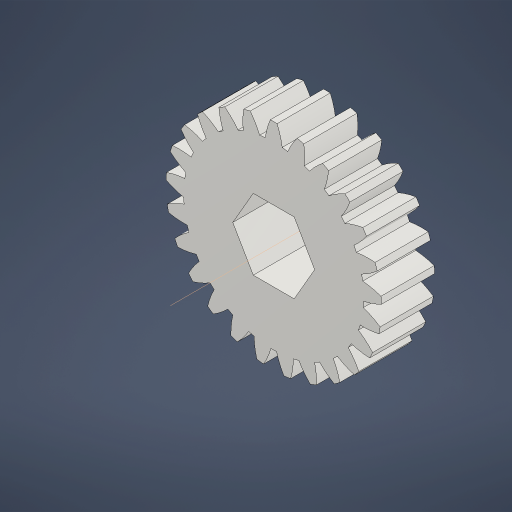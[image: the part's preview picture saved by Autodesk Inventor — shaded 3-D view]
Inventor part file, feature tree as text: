
AUTODESK INVENTOR PART (.ipt)
format: ipt  version: 2024.3 (Build 283343000, 343)  size: 343,552 bytes
history: native  units: mm (DEFAULTED — no unit token found)
features: plane x3, other x3, extrude x2, sketch x2
ambient origin geometry x8: Origin, YZ Plane, XZ Plane, XY Plane, X Axis, Y Axis, Z Axis, Center Point
bodies: Solid1 (feature_tree)
feature tree (10):
  extrude  "Extrusion1"  Depth=9.525mm TaperAngle=0.0deg
  plane  "Work Plane1"
  plane  "Work Plane2"
  plane  "Work Plane3"
  other  "Spur Gear"
  extrude  "Extrusion2"  Depth=12.7mm TaperAngle=0.0deg
  sketch  "Sketch1"  dims[d0=38.593216mm d1=9.525mm d2=0.0mm]
  other  "Srf1"
  sketch  "Sketch3"  dims[d3=35.277778mm d4=76.2mm d5=0.0mm d6=0.0mm d7=1.256637mm d9=0.0mm d14=0.0mm d15=88.441052mm d16=0.0mm d17=0.0mm d18=0.0mm d19=88.441052mm d20=12.7mm d21=0.0mm d22=0.0mm]
  other  "Pitch Diameter"
